# Revit family: Taktila - Farefelt - NCS8000
name_source: partatom
category: Generic Models
units: mm (PartAtom-declared; Revit-internal decimal feet)

## family parameters
Can host rebar = No
Cut with Voids When Loaded = No
Host = Face
Maintain Annotation Orientation = No
Part Type = Normal
Room Calculation Point = No
Round Connector Dimension = Use Diameter
Shared = No

## types (16) — shared parameters
Bracket_Spacing = 95 mm  [stored 0.31168 ft]
zero-valued in all types: Default Elevation

## per-type parameters (varying)
| type | Number_of_Brackets_1 | Number_of_Brackets_2 | Width |
| 500mm | 6 | 5 | 500 mm  [stored 1.64042 ft] |
| 600mm | 7 | 6 | 600 mm |
| 700mm | 8 | 7 | 700 mm  [stored 2.29659 ft] |
| 800mm | 9 | 8 | 800 mm  [stored 2.62467 ft] |
| 900mm | 10 | 9 | 900 mm  [stored 2.95276 ft] |
| 1000mm | 11 | 11 | 1000 mm  [stored 3.28084 ft] |
| 1100mm | 12 | 12 | 1100 mm |
| 1200mm | 13 | 13 | 1200 mm |
| 1300mm | 14 | 14 | 1300 mm  [stored 4.26509 ft] |
| 1400mm | 15 | 15 | 1400 mm  [stored 4.59318 ft] |
| 1500mm | 16 | 16 | 1500 mm  [stored 4.92126 ft] |
| 1600mm | 17 | 17 | 1600 mm  [stored 5.24934 ft] |
| 1700mm | 18 | 18 | 1700 mm  [stored 5.57743 ft] |
| 1800mm | 19 | 19 | 1800 mm  [stored 5.90551 ft] |
| 1900mm | 20 | 20 | 1900 mm  [stored 6.2336 ft] |
| 2000mm | 22 | 21 | 2000 mm  [stored 6.56168 ft] |

note: [stored X ft] marks values corroborated as IEEE doubles in the binary element streams (Revit-internal decimal feet)

## geometry (parser evidence)
native form markers: Sweep x5
no freeform markers — native parametric forms only
